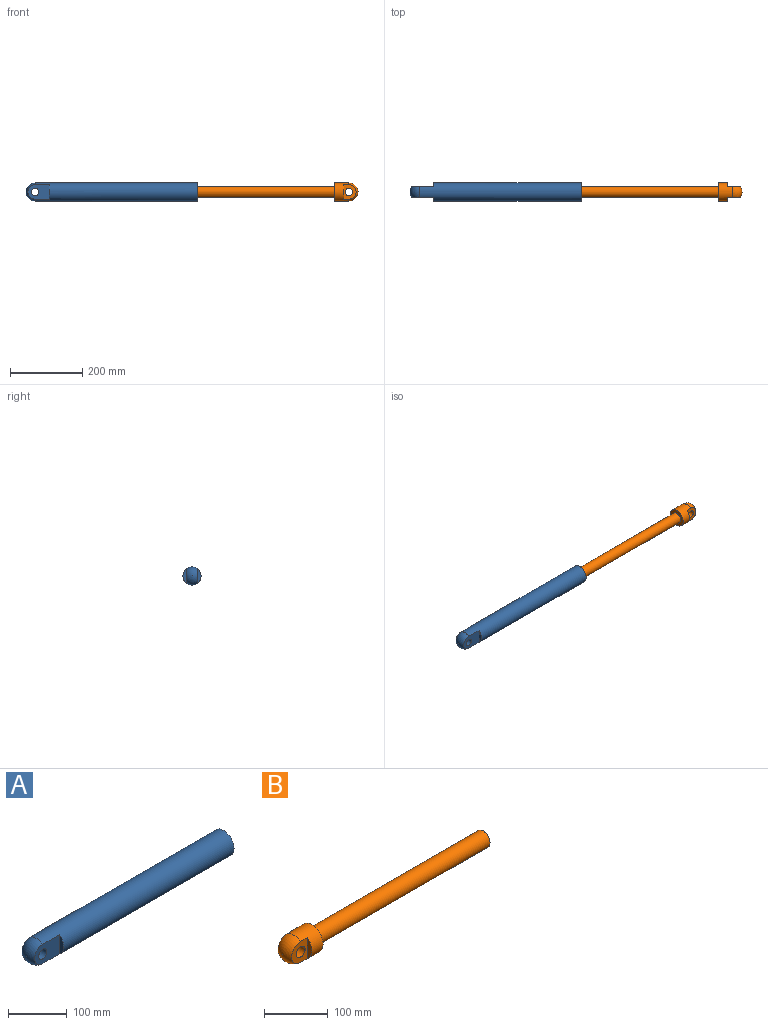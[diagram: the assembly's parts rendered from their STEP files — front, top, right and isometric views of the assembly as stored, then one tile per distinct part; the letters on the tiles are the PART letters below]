
ASSEMBLY  parts=2 mates=1
PART A: 10 faces, bbox 475x50x50 mm
  f0: sphere r=25mm, area 2356.2mm2, adj f1,f6,f8
  f1: cylinder r=25mm len=450mm, axis (1,0,0), area 66976.7mm2, adj f0,f4,f5,f6,f7,f8
  f2: plane 30x30mm, normal (1,0,0), area 706.9mm2, adj f3
  f3: cylinder r=15mm len=380mm, axis (1,0,0), area 35814.2mm2, adj f2,f4
  f4: plane 50x50mm, normal (1,0,0), area 1256.6mm2, adj f1,f3
  f5: plane 40x10mm, normal (-1,0,0), area 279.6mm2, adj f1,f6
  f6: plane 60x40mm, normal (0,-1,0), area 1914.2mm2, adj f0,f1,f5,f9
  f7: plane 40x10mm, normal (-1,0,0), area 279.6mm2, adj f1,f8
  f8: plane 60x40mm, normal (0,1,0), area 1914.2mm2, adj f0,f1,f7,f9
  f9: cylinder r=10mm len=30mm, axis (0,-1,0), area 1885mm2, adj f6,f8
PART B: 10 faces, bbox 445x50x50 mm
  f0: sphere r=25mm, area 2356.2mm2, adj f1,f6,f7
  f1: cylinder r=25mm len=50mm, axis (-1,0,0), area 4892.2mm2, adj f0,f4,f5,f6,f7,f8
  f2: plane 30x30mm, normal (1,0,0), area 706.9mm2, adj f3
  f3: cylinder r=15mm len=380mm, axis (-1,0,0), area 35814.2mm2, adj f2,f4
  f4: plane 50x50mm, normal (1,0,0), area 1256.6mm2, adj f1,f3
  f5: plane 40x10mm, normal (-1,0,0), area 279.6mm2, adj f1,f6
  f6: plane 40x35mm, normal (0,-1,0), area 914.2mm2, adj f0,f1,f5,f9
  f7: plane 40x35mm, normal (0,1,0), area 914.2mm2, adj f0,f1,f8,f9
  f8: plane 40x10mm, normal (-1,0,0), area 279.6mm2, adj f1,f7
  f9: cylinder r=10mm len=30mm, axis (0,-1,0), area 1885mm2, adj f6,f7
PLACE A rot(axis=(0.37,0.21,0.91),0deg) t=(-304.38,-132.46,64.92)mm fixed
PLACE B rot(axis=(0,-1,0),180deg) t=(565.62,-32.46,64.92)mm
MATE slider B.f1 <-> A.f1  axis (-1,0,0) through (145.62,-132.46,64.92)mm
